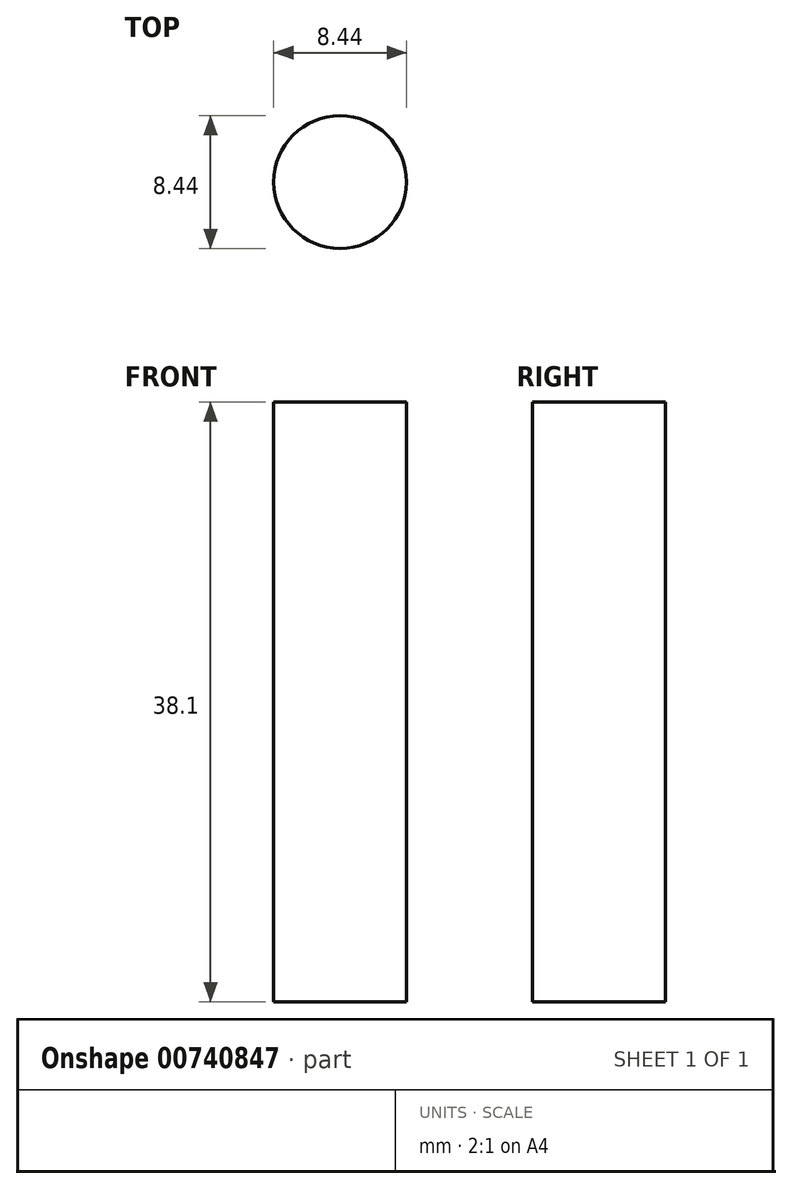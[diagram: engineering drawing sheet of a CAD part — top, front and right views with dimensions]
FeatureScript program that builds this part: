
annotation { "Feature Type Name" : "Feature", "Feature Type Description" : "" }
export const myFeature = defineFeature(function(context is Context, id is Id, definition is map)
    precondition{}
    {
        {
            var Q0;
            Q0=qCreatedBy(makeId("Top.planeOp"),FACE);
            var sketch = newSketch(context, id + "F0", { "sketchPlane" : qUnion([Q0])});
            skCircle(sketch, "E0", {"center": v(0, 0) * mm, "radius": 4.22 * mm});
            skSolve(sketch);
        }
        {
            var Q0;
            Q0 = qSketchRegion(id + "F0", true);
            extrude(context, id + "F1", {"entities" : qUnion([Q0]), "depth" : 38.1 * mm, "offsetDistance" : 25.4 * mm});
        }
    });
